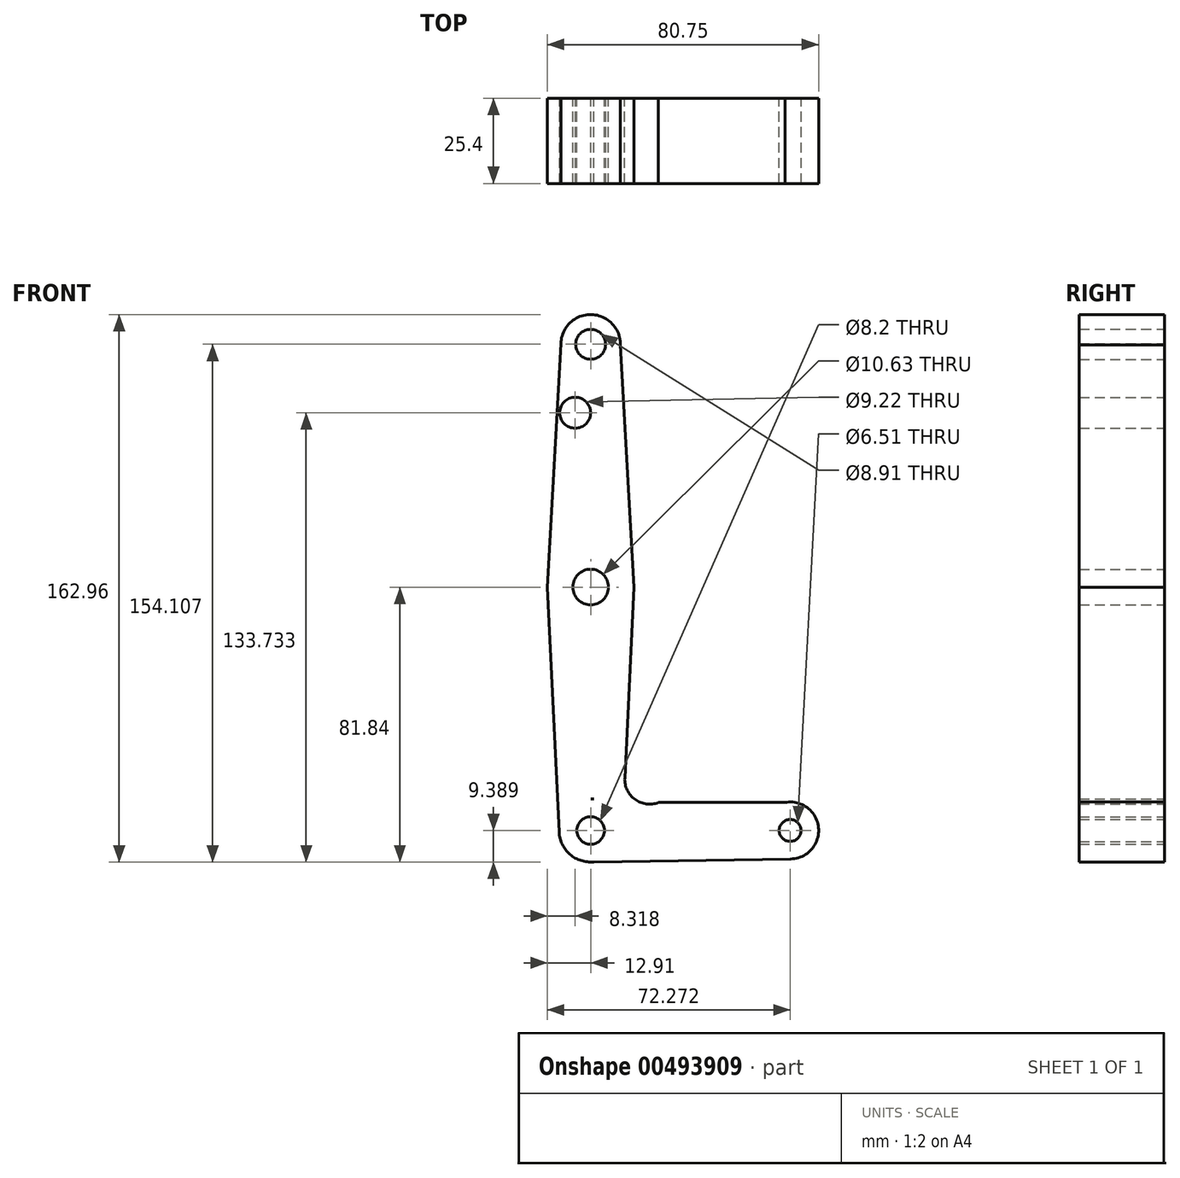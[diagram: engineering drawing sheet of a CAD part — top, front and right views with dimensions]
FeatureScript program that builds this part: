
annotation { "Feature Type Name" : "Feature", "Feature Type Description" : "" }
export const myFeature = defineFeature(function(context is Context, id is Id, definition is map)
    precondition{}
    {
        {
            var Q0;
            Q0=qCreatedBy(makeId("Front.planeOp"),FACE);
            var sketch = newSketch(context, id + "F0", { "sketchPlane" : qUnion([Q0])});
            skLineSegment(sketch, "E0", {"start": v(0, 0) * mm, "end": v(0, 72.27) * mm});
            skLineSegment(sketch, "E1", {"start": v(0, 72.27) * mm, "end": v(0, 0) * mm});
            skLineSegment(sketch, "E2", {"start": v(0, -63.06) * mm, "end": v(0, 0) * mm});
            skCircle(sketch, "E3", {"center": v(0, 72.27) * mm, "radius": 8.85 * mm});
            skCircle(sketch, "E4", {"center": v(0, 0) * mm, "radius": 12.9 * mm});
            skCircle(sketch, "E5", {"center": v(0, -72.45) * mm, "radius": 9.4 * mm});
            skLineSegment(sketch, "E6", {"start": v(-8.82, 73.08) * mm, "end": v(-12.91, 0) * mm});
            skLineSegment(sketch, "E7", {"start": v(-12.91, 0) * mm, "end": v(-9.38, -72.9) * mm});
            skLineSegment(sketch, "E8", {"start": v(8.85, 72.02) * mm, "end": v(12.91, 0) * mm});
            skLineSegment(sketch, "E9", {"start": v(12.91, 0) * mm, "end": v(10.16, -56.88) * mm});
            skLineSegment(sketch, "E10", {"start": v(0, -81.84) * mm, "end": v(0.9, -81.8) * mm});
            skLineSegment(sketch, "E11", {"start": v(0, -63.06) * mm, "end": v(0.98, -63.11) * mm});
            skArc(sketch, "E12", {"start": v(10.16, -56.88) * mm, "mid": v(13.2, -63.21) * mm, "end": v(20.18, -64.12) * mm});
            skLineSegment(sketch, "E13", {"start": v(55.27, -65.02) * mm, "end": v(56.1, -65.04) * mm});
            skCircle(sketch, "E14", {"center": v(0, 72.27) * mm, "radius": 4.46 * mm});
            skCircle(sketch, "E15", {"center": v(0, 0) * mm, "radius": 5.31 * mm});
            skCircle(sketch, "E16", {"center": v(0, -72.45) * mm, "radius": 4.1 * mm});
            skCircle(sketch, "E17", {"center": v(59.36, -72.45) * mm, "radius": 3.26 * mm});
            skCircle(sketch, "E18", {"center": v(-4.6, 51.9) * mm, "radius": 4.6 * mm});
            skPoint(sketch, "E19.end.orphan", {"position": v(65.68, -65.04) * mm});
            skCircle(sketch, "E20", {"center": v(59.36, -72.45) * mm, "radius": 8.48 * mm});
            skLineSegment(sketch, "E21.trimOffspring", {"start": v(54.25, -79.22) * mm, "end": v(54.87, -79.19) * mm});
            skLineSegment(sketch, "E22", {"start": v(0.9, -81.8) * mm, "end": v(59.49, -80.93) * mm});
            skLineSegment(sketch, "E23", {"start": v(20.18, -64.12) * mm, "end": v(60.94, -64.12) * mm});
            skSolve(sketch);
        }
        {
            var Q0;
            Q0 = qSketchRegion(id + "F0", true);
            extrude(context, id + "F1", {"entities" : qUnion([Q0]), "depth" : 25.4 * mm});
        }
    });
